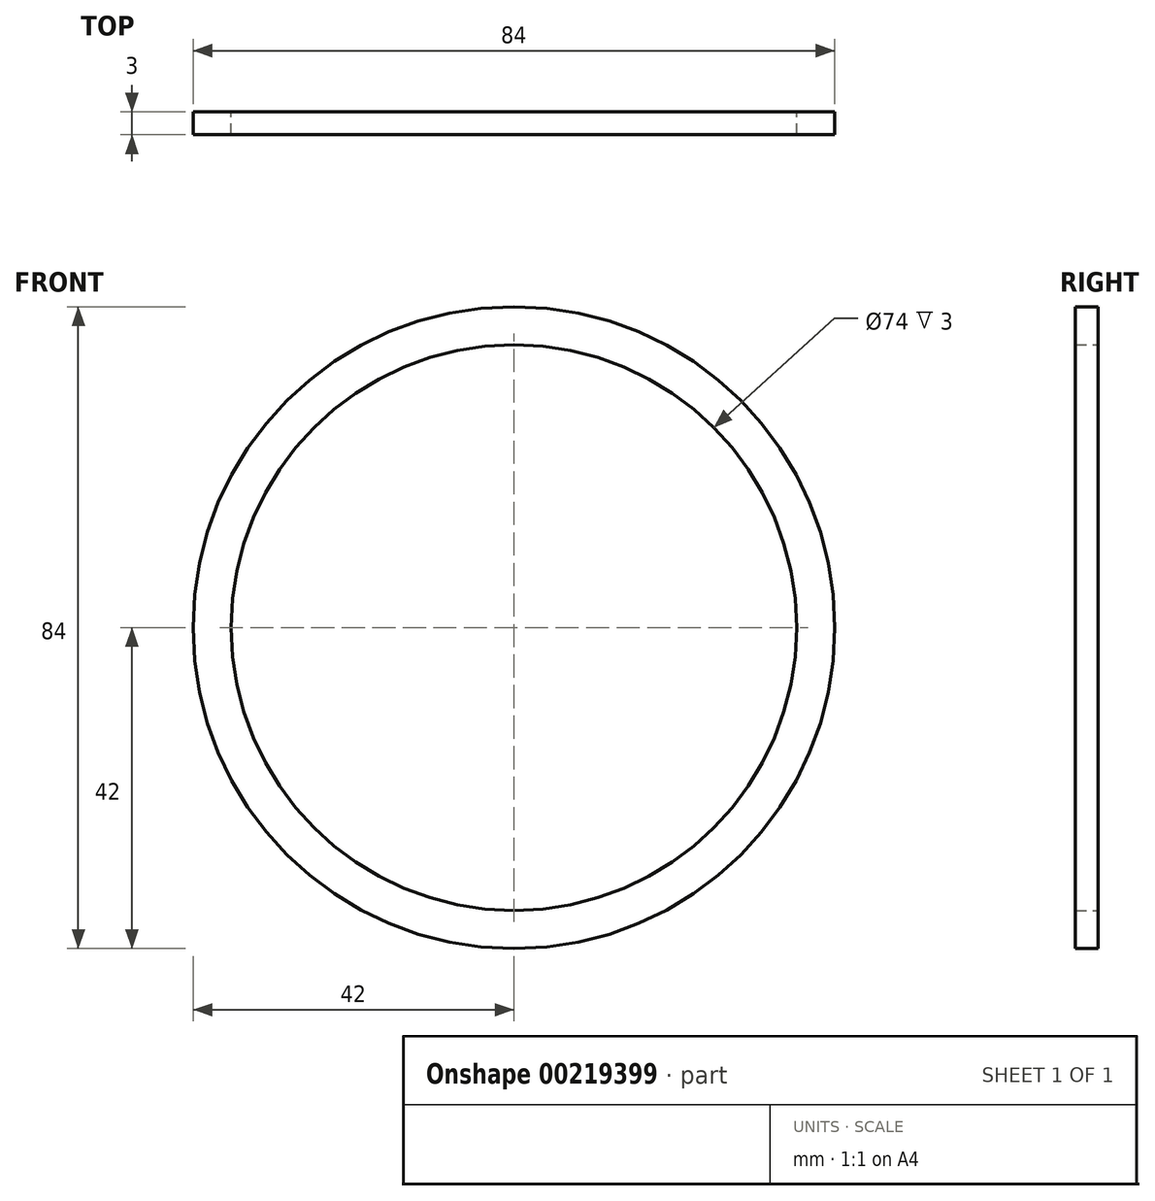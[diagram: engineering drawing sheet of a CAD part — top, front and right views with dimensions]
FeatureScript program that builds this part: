
annotation { "Feature Type Name" : "Feature", "Feature Type Description" : "" }
export const myFeature = defineFeature(function(context is Context, id is Id, definition is map)
    precondition{}
    {
        {
            var Q0;
            Q0=qCreatedBy(makeId("Front.planeOp"),FACE);
            var sketch = newSketch(context, id + "F0", { "sketchPlane" : qUnion([Q0])});
            skCircle(sketch, "E0", {"center": v(0, 0) * mm, "radius": 37 * mm});
            skCircle(sketch, "E1", {"center": v(0, 0) * mm, "radius": 42 * mm});
            skSolve(sketch);
        }
        {
            var Q0;
            Q0=makeQuery(id+"F0.imprint","IMPRINT",FACE,{"disambiguationData":[TD([[makeQuery(id+"F0.imprint","IMPRINT",EDGE,{"derivedFrom":sQuery(id+"F0.wireOp",EDGE,"E0")}),-1.0]])]});
            extrude(context, id + "F1", {"entities" : qUnion([Q0]), "depth" : 3 * mm});
        }
    });
